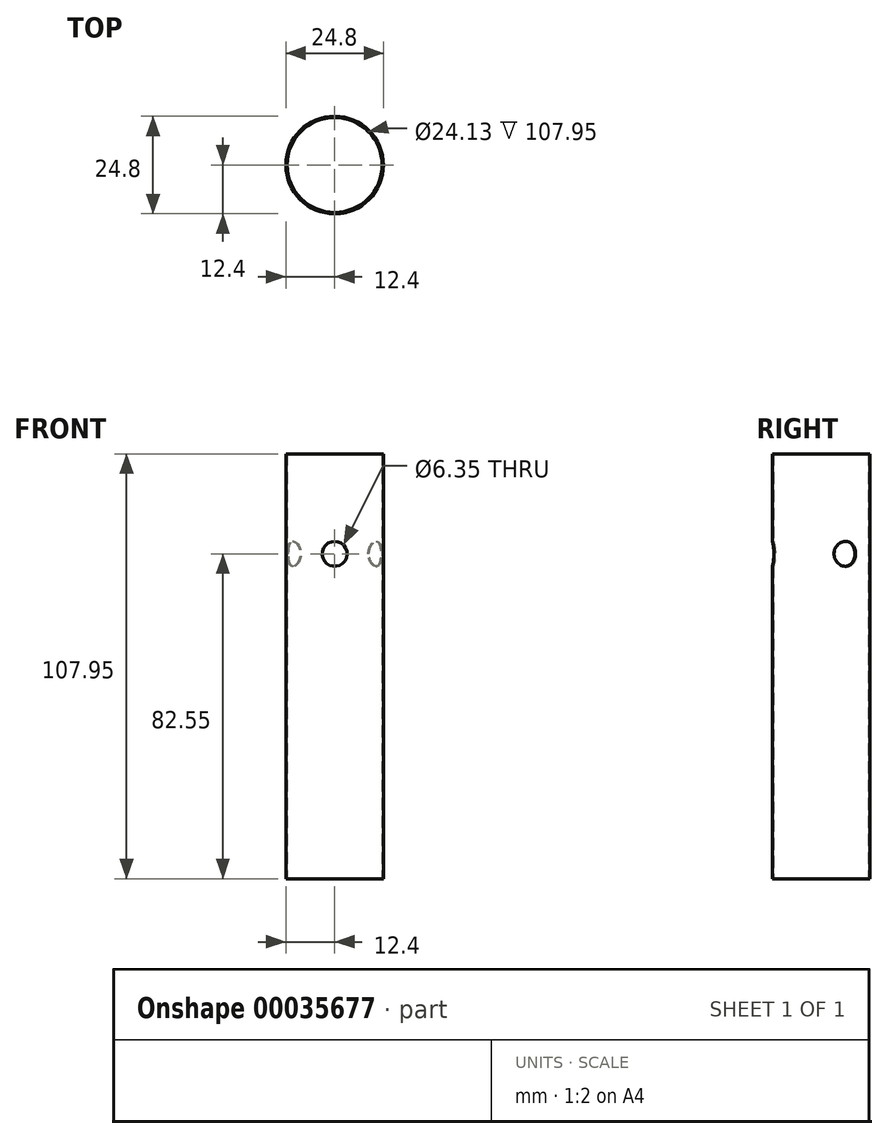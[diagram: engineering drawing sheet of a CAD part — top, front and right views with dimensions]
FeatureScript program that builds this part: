
annotation { "Feature Type Name" : "Feature", "Feature Type Description" : "" }
export const myFeature = defineFeature(function(context is Context, id is Id, definition is map)
    precondition{}
    {
        {
            var Q0;
            Q0=qCreatedBy(makeId("Front.planeOp"),FACE);
            var sketch = newSketch(context, id + "F0", { "sketchPlane" : qUnion([Q0])});
            skLineSegment(sketch, "E0", {"start": v(0, 0) * mm, "end": v(0, 107.95) * mm});
            skLineSegment(sketch, "E1", {"start": v(0, 107.95) * mm, "end": v(12.06, 107.95) * mm});
            skLineSegment(sketch, "E2", {"start": v(12.06, 107.95) * mm, "end": v(12.07, 0) * mm});
            skLineSegment(sketch, "E3", {"start": v(12.07, 0) * mm, "end": v(0, 0) * mm});
            skLineSegment(sketch, "E4", {"start": v(12.06, 0) * mm, "end": v(12.4, 0) * mm});
            skLineSegment(sketch, "E5", {"start": v(12.4, 0) * mm, "end": v(12.4, 107.95) * mm});
            skLineSegment(sketch, "E6", {"start": v(12.4, 107.95) * mm, "end": v(12.06, 107.95) * mm});
            skSolve(sketch);
        }
        {
            var Q0;
            Q0=makeQuery(id+"F0.imprint","IMPRINT",FACE,{"disambiguationData":[TD([[makeQuery(id+"F0.imprint","IMPRINT",EDGE,{"derivedFrom":sQuery(id+"F0.wireOp",EDGE,"E2")}),1.0]])]});
            var Q1;
            Q1=sQuery(id+"F0.wireOp",EDGE,"E0");
            revolve(context, id + "F1", {"entities" : qUnion([Q0]), "axis" : qUnion([Q1]), "revolveType" : RevolveType.FULL});
        }
        {
            var Q0;
            Q0=qCreatedBy(makeId("Front.planeOp"),FACE);
            var sketch = newSketch(context, id + "F2", { "sketchPlane" : qUnion([Q0])});
            skLineSegment(sketch, "E7", {"start": v(0, 0) * mm, "end": v(0, 107.95) * mm, "construction": true});
            skCircle(sketch, "E8", {"center": v(0, 82.55) * mm, "radius": 3.18 * mm});
            skPoint(sketch, "E9", {"position": v(0, 85.72) * mm});
            skSolve(sketch);
        }
        {
            var Q0;
            Q0 = qSketchRegion(id + "F2", true);
            extrude(context, id + "F3", {"entities" : qUnion([Q0]), "operationType" : NewBodyOperationType.REMOVE, "endBound" : BoundingType.THROUGH_ALL, "depth" : 25.4 * mm});
        }
        {
            var Q0;
            Q0=qCreatedBy(makeId("Top.planeOp"),FACE);
            var sketch = newSketch(context, id + "F4", { "sketchPlane" : qUnion([Q0])});
            skCircle(sketch, "E10.0", {"center": v(0, 0) * mm, "radius": 12.4 * mm});
            skLineSegment(sketch, "E11", {"start": v(0, 0) * mm, "end": v(0, 12.4) * mm});
            skLineSegment(sketch, "E12", {"start": v(0, 0) * mm, "end": v(0, -12.4) * mm});
            skLineSegment(sketch, "E13", {"start": v(0, 0) * mm, "end": v(10.73, -6.2) * mm});
            skLineSegment(sketch, "E14.MirrorCS", {"start": v(0, 0) * mm, "end": v(-10.73, -6.2) * mm});
            skLineSegment(sketch, "E15", {"start": v(0, 0) * mm, "end": v(-10.73, 6.2) * mm});
            skLineSegment(sketch, "E16", {"start": v(0, 0) * mm, "end": v(10.73, 6.2) * mm});
            skSolve(sketch);
        }
        {
            var Q0;
            Q0=sQuery(id+"F4.wireOp",EDGE,"E16");
            var Q1;
            Q1=sQuery(id+"F4.wireOp",VERTEX,"E16.end");
            cPlane(context, id + "F5", {"entities" : qUnion([Q0, Q1]), "cplaneType" : CPlaneType.CURVE_POINT, "offset" : 152.4 * mm, "width" : 152.4 * mm, "height" : 152.4 * mm});
        }
        {
            var Q0;
            Q0=qCreatedBy(id+"F5.planeOp",FACE);
            var sketch = newSketch(context, id + "F6", { "sketchPlane" : qUnion([Q0])});
            skLineSegment(sketch, "E17", {"start": v(0, 0) * mm, "end": v(0, 107.95) * mm, "construction": true});
            skCircle(sketch, "E18", {"center": v(0, 82.55) * mm, "radius": 3.18 * mm});
            skSolve(sketch);
        }
        {
            var Q0;
            Q0 = qSketchRegion(id + "F6", true);
            var Q1;
            Q1=makeQuery(id+"F1.opRevolve","SWEPT_FACE",FACE,{"disambiguationData":[OSD([sQuery(id+"F0.wireOp",EDGE,"E2")])]});
            extrude(context, id + "F7", {"entities" : qUnion([Q0]), "operationType" : NewBodyOperationType.REMOVE, "endBound" : BoundingType.UP_TO_SURFACE, "oppositeDirection" : true, "endBoundEntityFace" : qUnion([Q1]), "depth" : 25.4 * mm});
        }
        {
            var Q0;
            Q0=sQuery(id+"F4.wireOp",EDGE,"E15");
            var Q1;
            Q1=sQuery(id+"F4.wireOp",VERTEX,"E15.end");
            cPlane(context, id + "F8", {"entities" : qUnion([Q0, Q1]), "cplaneType" : CPlaneType.CURVE_POINT, "offset" : 152.4 * mm, "width" : 152.4 * mm, "height" : 152.4 * mm});
        }
        {
            var Q0;
            Q0=qCreatedBy(id+"F8.planeOp",FACE);
            var sketch = newSketch(context, id + "F9", { "sketchPlane" : qUnion([Q0])});
            skLineSegment(sketch, "E19", {"start": v(0, 0) * mm, "end": v(0, 107.95) * mm});
            skCircle(sketch, "E20", {"center": v(0, 82.55) * mm, "radius": 3.18 * mm});
            skSolve(sketch);
        }
        {
            var Q0;
            Q0 = qSketchRegion(id + "F9", true);
            var Q1;
            Q1=makeQuery(id+"F1.opRevolve","SWEPT_FACE",FACE,{"disambiguationData":[OSD([sQuery(id+"F0.wireOp",EDGE,"E2")])]});
            extrude(context, id + "F10", {"entities" : qUnion([Q0]), "operationType" : NewBodyOperationType.REMOVE, "endBound" : BoundingType.UP_TO_SURFACE, "oppositeDirection" : true, "endBoundEntityFace" : qUnion([Q1]), "depth" : 25.4 * mm});
        }
    });
